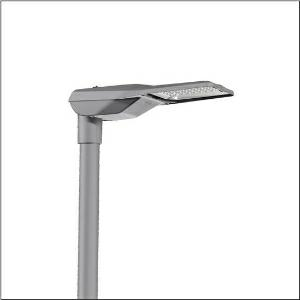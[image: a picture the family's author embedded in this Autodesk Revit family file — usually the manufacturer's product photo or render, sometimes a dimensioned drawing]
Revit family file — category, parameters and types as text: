
# Revit family: streetlight_sl_21_mini___st0_5a_5xe2b43s08gb_d1ce
name_source: partatom
category: Lighting Fixtures
units: mm (PartAtom-declared; Revit-internal decimal feet)

## family parameters
Cut with Voids When Loaded = No
Host = Face
Light Source = No
Part Type = Normal
Room Calculation Point = No
Round Connector Dimension = Use Diameter
Shared = No

## types (1)
- --- (1 x LED, 6180 lm, 40.4 W, 4000K)
    Apparent Load = 40 VA
    CIE Flux Codes = 41 75 97 100 100
    Color Rendering = 70
    Color Temperature = 4000K
    Default Elevation = 1800 mm
    Description = Streetlight SL 21 mini, mast luminaire, primary light control with lens, of PMMA, primary optical cover: cover, of toughened safety glass, transparent, light distribution: ST0.5a, light emission: direct distribution, primary light characteristic: asymmetric, installation type: side-entry, post-top, LED, High Power LED, rated luminous flux: 6.180lm, luminous efficacy: 153lm/W, light colour: 740, colour temperature: 4000K, control gear: D4i, control: overheat protection, constant luminous flux control, time-dependent luminous flux control, flexible luminous flux parameterisation, pre-setting: logarithmic dimming characteristic, mains connection: 220..240V, AC, 50/60Hz, start of lifetime: 40W, end of service life: 41W, reduction: 19W, luminaire housing, of diecast aluminium, powder-coated, Siteco® metallic grey (DB 702S), corrosivity category C5 mid according to DIN EN ISO 12944, please order mast flange separately, inclination adjustable: 0°, 5°, 10°, 15°, sealing non-destructively replaceable, multi-level sealing system, length: 628mm, width: 235mm, height: 110mm, mast flange for spigot size: 42mm (side-entry): 5XC10008XM4, 60/48mm (side-entry/post-top): 5XC10108XM2, 76/60mm (side-entry/post-top): 5XC10108XM1, mounting height: 4..8m, Smart Interface above, protection rating (complete): IP66, insulation class (complete): insulation class II (safety insulation), certification: CE, ENEC, ENEC+, VDE, impact resistance: IK10, permissible operating ambient temperature for outdoor applications: -40..+50°C, standard-compliant lighting for roads and squares, packaging unit: 1 piece

Light Distribution: ST0.5a
    Height = 110 mm
    Lamp = 1 x LED
    Lamp Light Flux = 6180 lm
    Lamp Power = 40.4 W
    Lamp count = 1
    Length = 625 mm
    Luminous efficacy = 153 lm/W
    Manufacturer = Siteco
    ModVariant = No
    Model = 5XE2B43S08GB
    Number of Poles = 1
    OnlyDefault = Yes
    Power Factor = 1
    Product Name = Streetlight SL 21 mini | ST0.5a
    Product group = mast luminaire | pylon top
    ProductGroupID = 6100
    Protection Class = Protection class II
    Protection Degree = IP 66
    RLX_Detail_Level = 1
    RLX_Emergency_Light_Flux = 0 lm
    RLX_Emergency_Type = 0
    RLX_Emergency_Type_DB = No
    RlxData = <blob elided: 37177 chars, md5=ecd9bb84>
    Socket = socket
    Standby Power = 0 W
    System Light Flux = 6180 lm
    System Power = 40 W
    Type Comments = factory setting: luminous flux: 100 % | dim-lin: 254 | 812 mA
    Type Image = l_1003515.jpg
    URL = http://relux.com
    VarID = @adj_191222
    Voltage = 0 V
    Weight = 0.00 kg
    Width = 234 mm

## geometry (parser evidence)
native form markers: Blend x4, Sweep x11
no freeform markers — native parametric forms only
